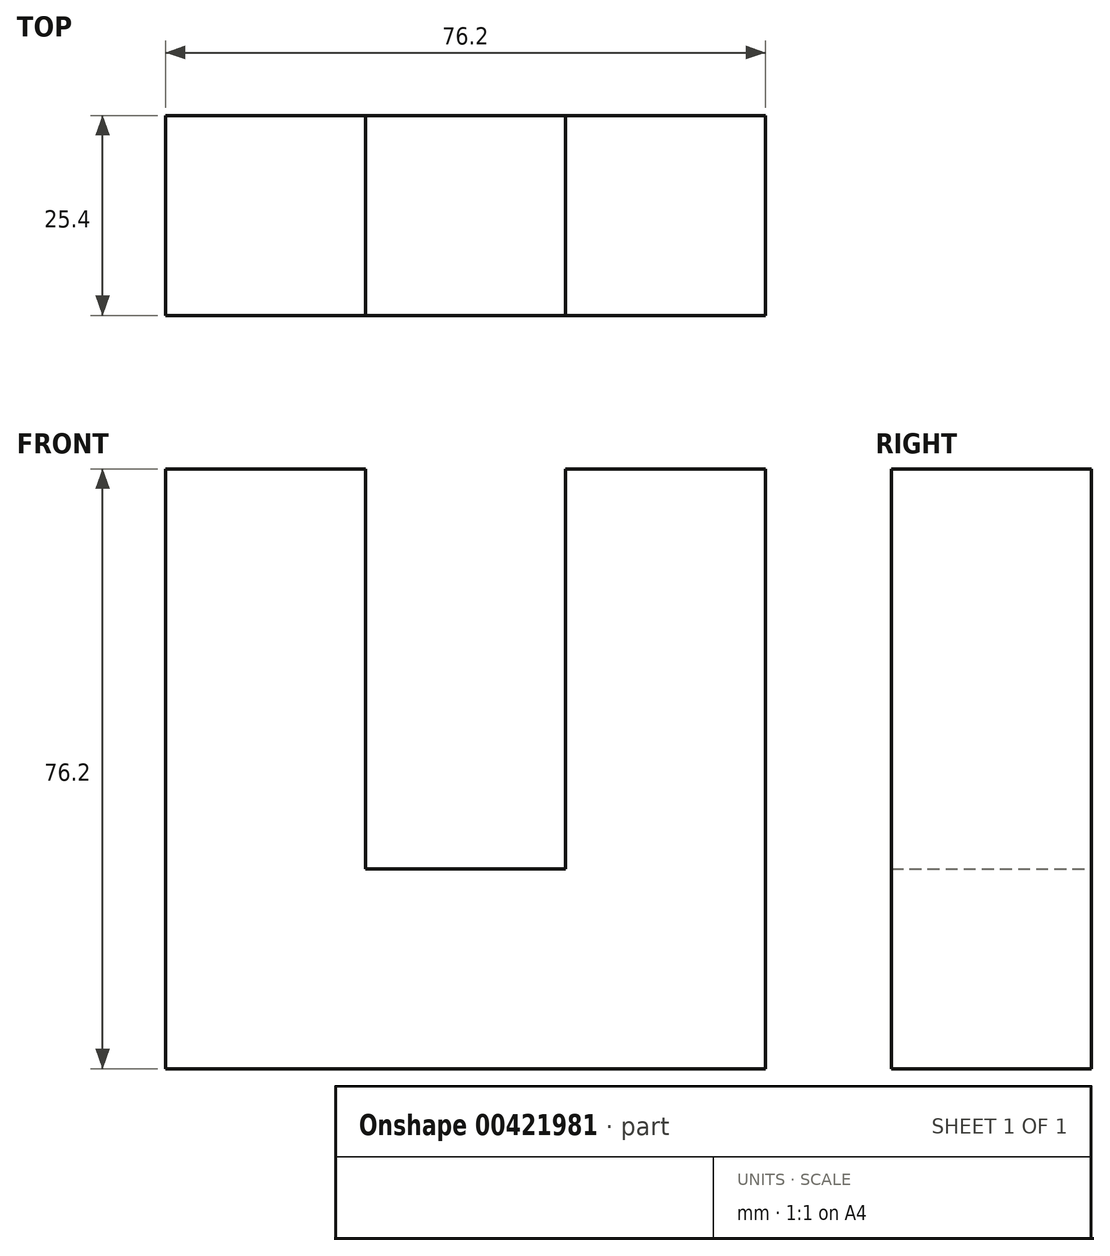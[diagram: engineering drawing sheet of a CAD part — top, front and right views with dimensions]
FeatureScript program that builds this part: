
annotation { "Feature Type Name" : "Feature", "Feature Type Description" : "" }
export const myFeature = defineFeature(function(context is Context, id is Id, definition is map)
    precondition{}
    {
        {
            var Q0;
            Q0=qCreatedBy(makeId("Front.planeOp"),FACE);
            var sketch = newSketch(context, id + "F0", { "sketchPlane" : qUnion([Q0])});
            skLineSegment(sketch, "E0", {"start": v(0, 0) * mm, "end": v(0, 76.2) * mm});
            skLineSegment(sketch, "E1", {"start": v(0, 0) * mm, "end": v(-76.2, 0) * mm});
            skLineSegment(sketch, "E2", {"start": v(-76.2, 0) * mm, "end": v(-76.2, 76.2) * mm});
            skLineSegment(sketch, "E3", {"start": v(-76.2, 76.2) * mm, "end": v(-50.8, 76.2) * mm});
            skLineSegment(sketch, "E4", {"start": v(-50.8, 76.2) * mm, "end": v(-50.8, 25.4) * mm});
            skLineSegment(sketch, "E5", {"start": v(-50.8, 25.4) * mm, "end": v(-25.4, 25.4) * mm});
            skLineSegment(sketch, "E6", {"start": v(-25.4, 25.4) * mm, "end": v(-25.4, 76.2) * mm});
            skLineSegment(sketch, "E7", {"start": v(-25.4, 76.2) * mm, "end": v(0, 76.2) * mm});
            skSolve(sketch);
        }
        {
            var Q0;
            Q0 = qSketchRegion(id + "F0", true);
            extrude(context, id + "F1", {"entities" : qUnion([Q0]), "depth" : 25.4 * mm});
        }
    });
